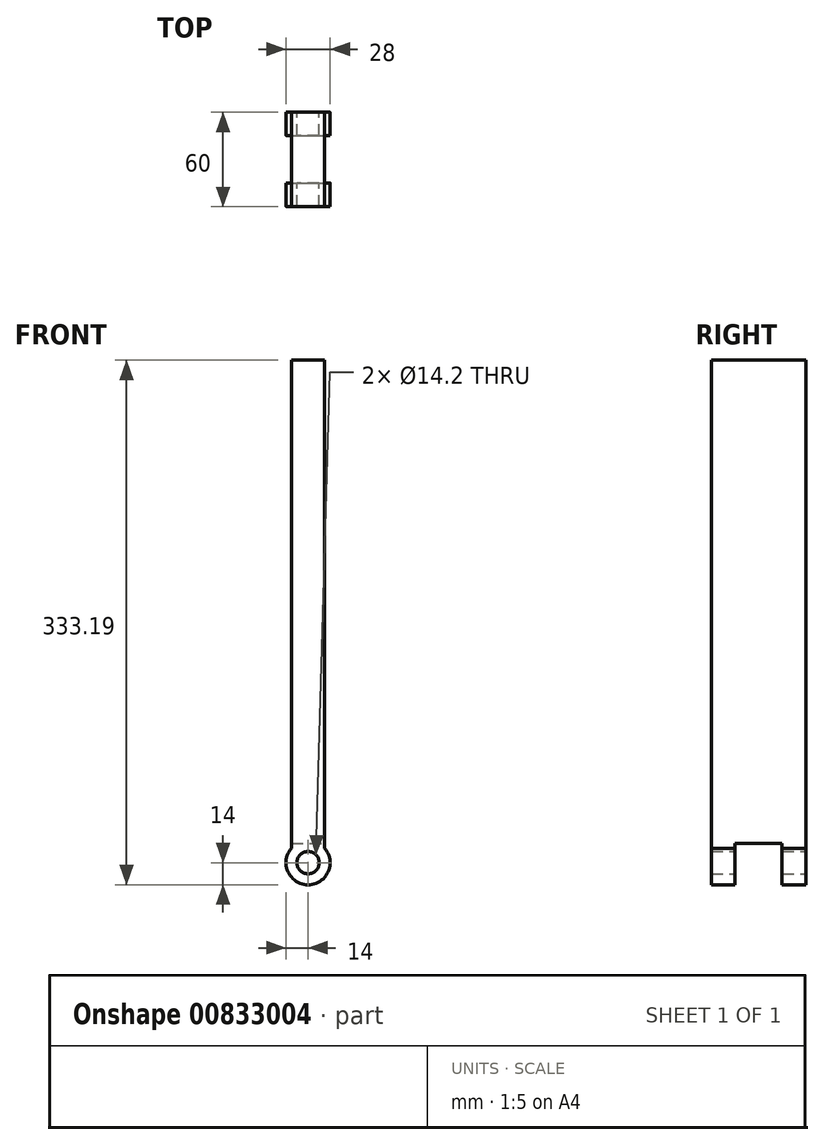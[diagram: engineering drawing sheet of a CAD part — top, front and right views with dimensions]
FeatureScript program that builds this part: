
annotation { "Feature Type Name" : "Feature", "Feature Type Description" : "" }
export const myFeature = defineFeature(function(context is Context, id is Id, definition is map)
    precondition{}
    {
        {
            var Q0;
            Q0=qCreatedBy(makeId("Front.planeOp"),FACE);
            var sketch = newSketch(context, id + "F0", { "sketchPlane" : qUnion([Q0])});
            skCircle(sketch, "E0", {"center": v(0, 0) * mm, "radius": 7.1 * mm});
            skArc(sketch, "E1", {"start": v(-10.56, 9.2) * mm, "mid": v(0, -14) * mm, "end": v(10.56, 9.2) * mm});
            skLineSegment(sketch, "E2.bottom", {"start": v(-10.56, 319.2) * mm, "end": v(10.56, 319.2) * mm});
            skLineSegment(sketch, "E2.left", {"start": v(-10.56, 319.2) * mm, "end": v(-10.56, 9.2) * mm});
            skLineSegment(sketch, "E2.right", {"start": v(10.56, 319.2) * mm, "end": v(10.56, 9.2) * mm});
            skPoint(sketch, "E2.middle", {"position": v(0, 164.2) * mm});
            skSolve(sketch);
        }
        {
            var Q0;
            Q0 = qSketchRegion(id + "F0", true);
            extrude(context, id + "F1", {"entities" : qUnion([Q0]), "depth" : 60 * mm, "offsetDistance" : 25 * mm});
        }
        {
            var Q0;
            Q0=qCreatedBy(makeId("Right.planeOp"),FACE);
            var sketch = newSketch(context, id + "F2", { "sketchPlane" : qUnion([Q0])});
            skLineSegment(sketch, "E3.bottom", {"start": v(-15, 12.38) * mm, "end": v(-45, 12.38) * mm});
            skLineSegment(sketch, "E3.top", {"start": v(-15, -14.67) * mm, "end": v(-45, -14.67) * mm});
            skLineSegment(sketch, "E3.left", {"start": v(-15, 12.38) * mm, "end": v(-15, -14.67) * mm});
            skLineSegment(sketch, "E3.right", {"start": v(-45, 12.38) * mm, "end": v(-45, -14.67) * mm});
            skSolve(sketch);
        }
        {
            var Q0;
            Q0 = qSketchRegion(id + "F2", true);
            extrude(context, id + "F3", {"entities" : qUnion([Q0]), "operationType" : NewBodyOperationType.REMOVE, "oppositeDirection" : true, "depth" : 25 * mm, "offsetDistance" : 25 * mm, "hasSecondDirection" : true, "secondDirectionOppositeDirection" : false, "secondDirectionDepth" : 25 * mm});
        }
    });
